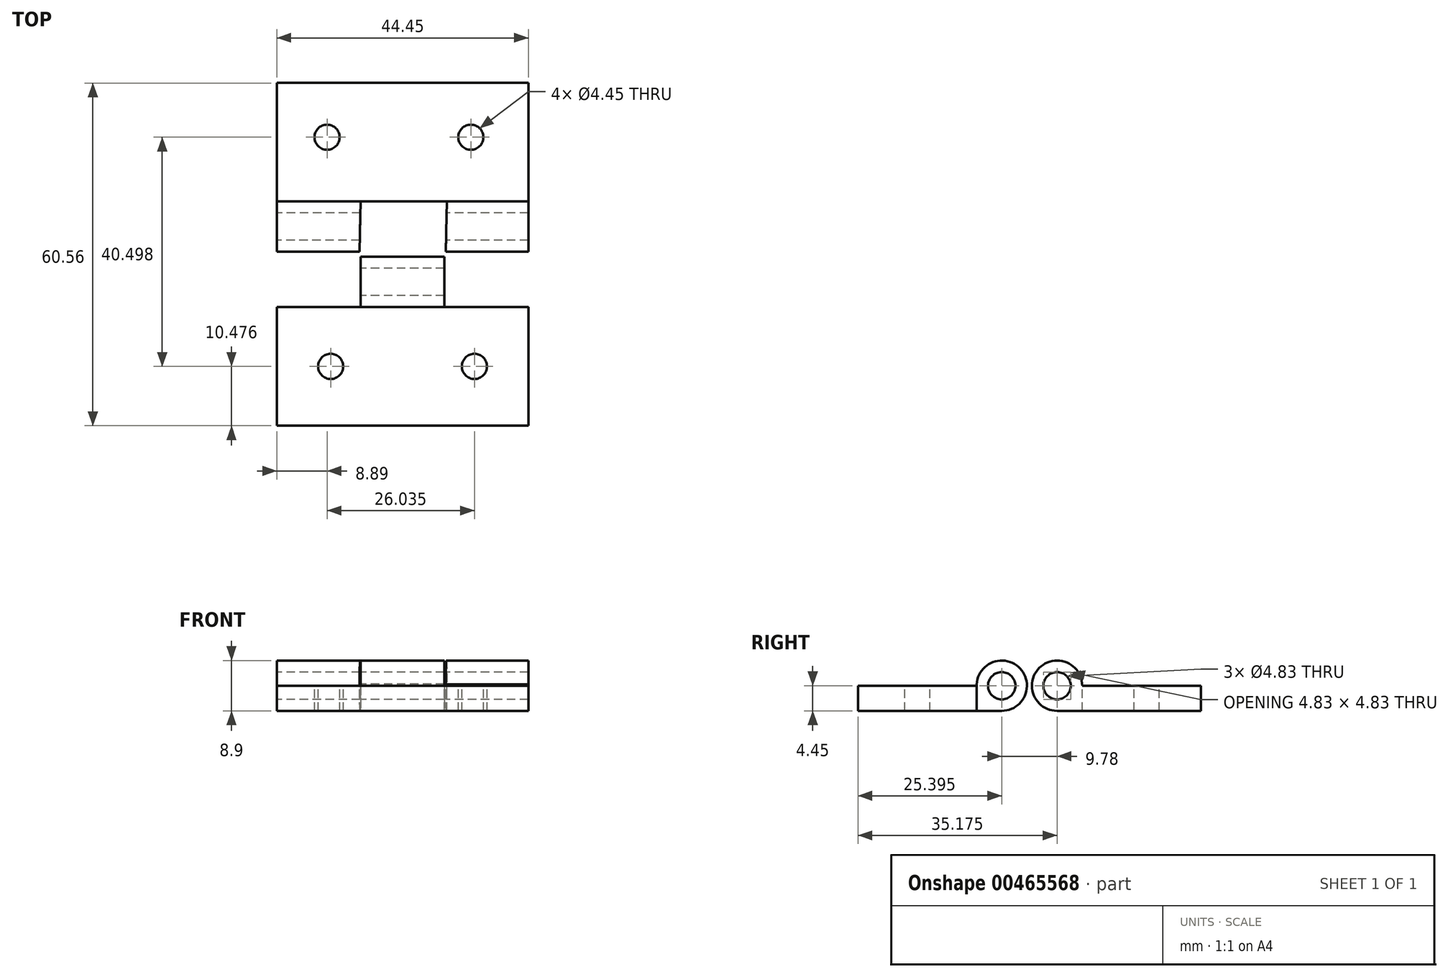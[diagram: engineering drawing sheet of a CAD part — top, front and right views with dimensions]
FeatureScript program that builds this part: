
annotation { "Feature Type Name" : "Feature", "Feature Type Description" : "" }
export const myFeature = defineFeature(function(context is Context, id is Id, definition is map)
    precondition{}
    {
        {
            var Q0;
            Q0=qCreatedBy(makeId("Top.planeOp"),FACE);
            var sketch = newSketch(context, id + "F0", { "sketchPlane" : qUnion([Q0])});
            skLineSegment(sketch, "E0.bottom", {"start": v(0, 5.21) * mm, "end": v(44.45, 5.21) * mm});
            skLineSegment(sketch, "E0.top", {"start": v(0, 30.61) * mm, "end": v(44.45, 30.61) * mm});
            skLineSegment(sketch, "E0.left", {"start": v(0, 5.21) * mm, "end": v(0, 30.61) * mm});
            skLineSegment(sketch, "E0.right", {"start": v(44.45, 5.21) * mm, "end": v(44.45, 30.61) * mm});
            skLineSegment(sketch, "E1.bottom", {"start": v(0, -4.55) * mm, "end": v(44.45, -4.55) * mm});
            skLineSegment(sketch, "E1.top", {"start": v(0, -29.95) * mm, "end": v(44.45, -29.95) * mm});
            skLineSegment(sketch, "E1.left", {"start": v(0, -4.55) * mm, "end": v(0, -29.95) * mm});
            skLineSegment(sketch, "E1.right", {"start": v(44.45, -4.55) * mm, "end": v(44.45, -29.95) * mm});
            skSolve(sketch);
        }
        {
            var Q0;
            Q0=qCreatedBy(makeId("Right.planeOp"),FACE);
            var sketch = newSketch(context, id + "F1", { "sketchPlane" : qUnion([Q0])});
            skCircle(sketch, "E2", {"center": v(5.22, 0) * mm, "radius": 4.45 * mm});
            skCircle(sketch, "E3", {"center": v(-4.56, 0) * mm, "radius": 4.45 * mm});
            skSolve(sketch);
        }
        {
            var Q0;
            Q0=makeQuery(id+"F0.imprint","IMPRINT",FACE,{"disambiguationData":[TD([[makeQuery(id+"F0.imprint","IMPRINT",EDGE,{"derivedFrom":sQuery(id+"F0.wireOp",EDGE,"E0.bottom")}),1.0]])]});
            extrude(context, id + "F2", {"entities" : qUnion([Q0]), "oppositeDirection" : true, "depth" : 4.44 * mm});
        }
        {
            var Q0;
            Q0=makeQuery(id+"F0.imprint","IMPRINT",FACE,{"disambiguationData":[TD([[makeQuery(id+"F0.imprint","IMPRINT",EDGE,{"derivedFrom":sQuery(id+"F0.wireOp",EDGE,"E1.bottom")}),-1.0]])]});
            extrude(context, id + "F3", {"entities" : qUnion([Q0]), "oppositeDirection" : true, "depth" : 4.44 * mm});
        }
        {
            var Q0;
            Q0=makeQuery(id+"F1.imprint","IMPRINT",FACE,{"disambiguationData":[TD([[makeQuery(id+"F1.imprint","IMPRINT",EDGE,{"derivedFrom":sQuery(id+"F1.wireOp",EDGE,"E2")}),1.0]])]});
            var Q1;
            Q1=makeQuery(id+"F1.imprint","IMPRINT",FACE,{"disambiguationData":[TD([[makeQuery(id+"F1.imprint","IMPRINT",EDGE,{"derivedFrom":sQuery(id+"F1.wireOp",EDGE,"E3")}),1.0]])]});
            extrude(context, id + "F4", {"entities" : qUnion([Q0, Q1]), "depth" : 44.45 * mm});
        }
        {
            var Q0;
            Q0=makeQuery(id+"F4.opExtrude","SWEPT_BODY",BODY,{"disambiguationData":[OSD([sQuery(id+"F1.wireOp",EDGE,"E2")])]});
            var Q1;
            Q1=makeQuery(id+"F2.opExtrude","SWEPT_BODY",BODY,{"disambiguationData":[OSD([sQuery(id+"F0.wireOp",EDGE,"E0.bottom"),sQuery(id+"F0.wireOp",EDGE,"E0.top"),sQuery(id+"F0.wireOp",EDGE,"E0.left"),sQuery(id+"F0.wireOp",EDGE,"E0.right")])]});
            var Q2;
            Q2=makeQuery(id+"F4.opExtrude","SWEPT_BODY",BODY,{"disambiguationData":[OSD([sQuery(id+"F1.wireOp",EDGE,"E3")])]});
            var Q3;
            Q3=makeQuery(id+"F3.opExtrude","SWEPT_BODY",BODY,{"disambiguationData":[OSD([sQuery(id+"F0.wireOp",EDGE,"E1.bottom"),sQuery(id+"F0.wireOp",EDGE,"E1.top"),sQuery(id+"F0.wireOp",EDGE,"E1.left"),sQuery(id+"F0.wireOp",EDGE,"E1.right")])]});
            booleanBodies(context, id + "F5", {"operationType" : BooleanOperationType.UNION, "tools" : qUnion([Q0, Q1, Q2, Q3])});
        }
        {
            var Q0;
            Q0=qCreatedBy(makeId("Top.planeOp"),FACE);
            var sketch = newSketch(context, id + "F6", { "sketchPlane" : qUnion([Q0])});
            skLineSegment(sketch, "E4.bottom", {"start": v(0, -0.11) * mm, "end": v(14.8, -0.11) * mm});
            skLineSegment(sketch, "E4.top", {"start": v(0, -9) * mm, "end": v(14.8, -9) * mm});
            skLineSegment(sketch, "E4.left", {"start": v(0, -0.11) * mm, "end": v(0, -9) * mm});
            skLineSegment(sketch, "E4.right", {"start": v(14.8, -0.11) * mm, "end": v(14.8, -9) * mm});
            skLineSegment(sketch, "E5.bottom", {"start": v(14.8, 9.66) * mm, "end": v(30.05, 9.66) * mm});
            skLineSegment(sketch, "E5.top", {"start": v(14.63, 0.77) * mm, "end": v(29.87, 0.77) * mm});
            skLineSegment(sketch, "E5.left", {"start": v(14.8, 9.66) * mm, "end": v(14.63, 0.77) * mm});
            skLineSegment(sketch, "E5.right", {"start": v(30.05, 9.66) * mm, "end": v(29.87, 0.77) * mm});
            skPoint(sketch, "E6.firstSnap0", {"position": v(29.96, 5.21) * mm});
            skLineSegment(sketch, "E6.bottom", {"start": v(29.62, -0.1) * mm, "end": v(44.48, -0.1) * mm});
            skLineSegment(sketch, "E6.top", {"start": v(29.62, -9) * mm, "end": v(44.48, -9) * mm});
            skLineSegment(sketch, "E6.left", {"start": v(29.62, -0.1) * mm, "end": v(29.62, -9) * mm});
            skLineSegment(sketch, "E6.right", {"start": v(44.48, -0.1) * mm, "end": v(44.48, -9) * mm});
            skSolve(sketch);
        }
        {
            var Q0;
            Q0=makeQuery(id+"F6.imprint","IMPRINT",FACE,{"disambiguationData":[TD([[makeQuery(id+"F6.imprint","IMPRINT",EDGE,{"derivedFrom":sQuery(id+"F6.wireOp",EDGE,"E4.bottom")}),-1.0]])]});
            var Q1;
            Q1=makeQuery(id+"F6.imprint","IMPRINT",FACE,{"disambiguationData":[TD([[makeQuery(id+"F6.imprint","IMPRINT",EDGE,{"derivedFrom":sQuery(id+"F6.wireOp",EDGE,"E6.bottom")}),-1.0]])]});
            extrude(context, id + "F7", {"entities" : qUnion([Q0, Q1]), "operationType" : NewBodyOperationType.REMOVE, "oppositeDirection" : true, "depth" : 5.08 * mm, "hasSecondDirection" : true, "secondDirectionOppositeDirection" : false, "secondDirectionDepth" : 5.08 * mm});
        }
        {
            var Q0;
            Q0=makeQuery(id+"F6.imprint","IMPRINT",FACE,{"disambiguationData":[TD([[makeQuery(id+"F6.imprint","IMPRINT",EDGE,{"derivedFrom":sQuery(id+"F6.wireOp",EDGE,"E5.bottom")}),-1.0]])]});
            extrude(context, id + "F8", {"entities" : qUnion([Q0]), "operationType" : NewBodyOperationType.REMOVE, "oppositeDirection" : true, "depth" : 5.08 * mm, "hasSecondDirection" : true, "secondDirectionOppositeDirection" : false, "secondDirectionDepth" : 5.08 * mm});
        }
        {
            var Q0;
            Q0=makeQuery(id+"F1.imprint","IMPRINT",FACE,{"disambiguationData":[TD([[makeQuery(id+"F1.imprint","IMPRINT",EDGE,{"derivedFrom":sQuery(id+"F1.wireOp",EDGE,"E2")}),1.0]])]});
            var sketch = newSketch(context, id + "F9", { "sketchPlane" : qUnion([Q0])});
            skCircle(sketch, "E7", {"center": v(-4.56, 0) * mm, "radius": 2.41 * mm});
            skSolve(sketch);
        }
        {
            var Q0;
            Q0=makeQuery(id+"F9.imprint","IMPRINT",FACE,{"disambiguationData":[TD([[makeQuery(id+"F9.imprint","IMPRINT",EDGE,{"derivedFrom":sQuery(id+"F9.wireOp",EDGE,"E7")}),1.0]])]});
            extrude(context, id + "F10", {"entities" : qUnion([Q0]), "operationType" : NewBodyOperationType.REMOVE, "endBound" : BoundingType.THROUGH_ALL, "depth" : 25.4 * mm});
        }
        {
            var Q0;
            Q0=makeQuery(id+"F1.imprint","IMPRINT",FACE,{"disambiguationData":[TD([[makeQuery(id+"F1.imprint","IMPRINT",EDGE,{"derivedFrom":sQuery(id+"F1.wireOp",EDGE,"E2")}),1.0]])]});
            var sketch = newSketch(context, id + "F11", { "sketchPlane" : qUnion([Q0])});
            skCircle(sketch, "E8", {"center": v(5.22, 0) * mm, "radius": 2.41 * mm});
            skSolve(sketch);
        }
        {
            var Q0;
            Q0=makeQuery(id+"F11.imprint","IMPRINT",FACE,{"disambiguationData":[TD([[makeQuery(id+"F11.imprint","IMPRINT",EDGE,{"derivedFrom":sQuery(id+"F11.wireOp",EDGE,"E8")}),1.0]])]});
            extrude(context, id + "F12", {"entities" : qUnion([Q0]), "operationType" : NewBodyOperationType.REMOVE, "endBound" : BoundingType.THROUGH_ALL, "depth" : 25.4 * mm});
        }
        {
            var Q0;
            Q0=makeQuery(id+"F2.opExtrude","CAP_FACE",FACE,{"disambiguationData":[OSD([sQuery(id+"F0.wireOp",EDGE,"E0.bottom"),sQuery(id+"F0.wireOp",EDGE,"E0.top"),sQuery(id+"F0.wireOp",EDGE,"E0.left"),sQuery(id+"F0.wireOp",EDGE,"E0.right")])],"isStart":true});
            var sketch = newSketch(context, id + "F13", { "sketchPlane" : qUnion([Q0])});
            skCircle(sketch, "E9", {"center": v(8.89, 21.02) * mm, "radius": 2.22 * mm});
            skCircle(sketch, "E10.1.0.0", {"center": v(34.29, 21.02) * mm, "radius": 2.22 * mm});
            skLineSegment(sketch, "E10.direction1", {"start": v(8.89, 21.02) * mm, "end": v(34.29, 21.02) * mm, "construction": true});
            skSolve(sketch);
        }
        {
            var Q0;
            Q0=makeQuery(id+"F13.imprint","IMPRINT",FACE,{"disambiguationData":[TD([[makeQuery(id+"F13.imprint","IMPRINT",EDGE,{"derivedFrom":sQuery(id+"F13.wireOp",EDGE,"E9")}),1.0]])]});
            var Q1;
            Q1=makeQuery(id+"F13.imprint","IMPRINT",FACE,{"disambiguationData":[TD([[makeQuery(id+"F13.imprint","IMPRINT",EDGE,{"derivedFrom":sQuery(id+"F13.wireOp",EDGE,"E10.1.0.0")}),1.0]])]});
            extrude(context, id + "F14", {"entities" : qUnion([Q0, Q1]), "operationType" : NewBodyOperationType.REMOVE, "endBound" : BoundingType.THROUGH_ALL, "oppositeDirection" : true, "depth" : 7.62 * mm, "hasSecondDirection" : true, "secondDirectionBound" : SecondDirectionBoundingType.THROUGH_ALL, "secondDirectionOppositeDirection" : false, "secondDirectionDepth" : 25.4 * mm});
        }
        {
            var Q0;
            Q0=makeQuery(id+"F3.opExtrude","CAP_FACE",FACE,{"disambiguationData":[OSD([sQuery(id+"F0.wireOp",EDGE,"E1.bottom"),sQuery(id+"F0.wireOp",EDGE,"E1.top"),sQuery(id+"F0.wireOp",EDGE,"E1.left"),sQuery(id+"F0.wireOp",EDGE,"E1.right")])],"isStart":true});
            var sketch = newSketch(context, id + "F15", { "sketchPlane" : qUnion([Q0])});
            skCircle(sketch, "E11", {"center": v(9.52, -19.47) * mm, "radius": 2.22 * mm});
            skCircle(sketch, "E12.1.0.0", {"center": v(34.92, -19.47) * mm, "radius": 2.22 * mm});
            skLineSegment(sketch, "E12.direction1", {"start": v(9.52, -19.47) * mm, "end": v(34.92, -19.47) * mm, "construction": true});
            skSolve(sketch);
        }
        {
            var Q0;
            Q0=makeQuery(id+"F15.imprint","IMPRINT",FACE,{"disambiguationData":[TD([[makeQuery(id+"F15.imprint","IMPRINT",EDGE,{"derivedFrom":sQuery(id+"F15.wireOp",EDGE,"E12.1.0.0")}),1.0]])]});
            var Q1;
            Q1=makeQuery(id+"F15.imprint","IMPRINT",FACE,{"disambiguationData":[TD([[makeQuery(id+"F15.imprint","IMPRINT",EDGE,{"derivedFrom":sQuery(id+"F15.wireOp",EDGE,"E11")}),1.0]])]});
            extrude(context, id + "F16", {"entities" : qUnion([Q0, Q1]), "operationType" : NewBodyOperationType.REMOVE, "endBound" : BoundingType.THROUGH_ALL, "oppositeDirection" : true, "depth" : 25.4 * mm});
        }
    });
